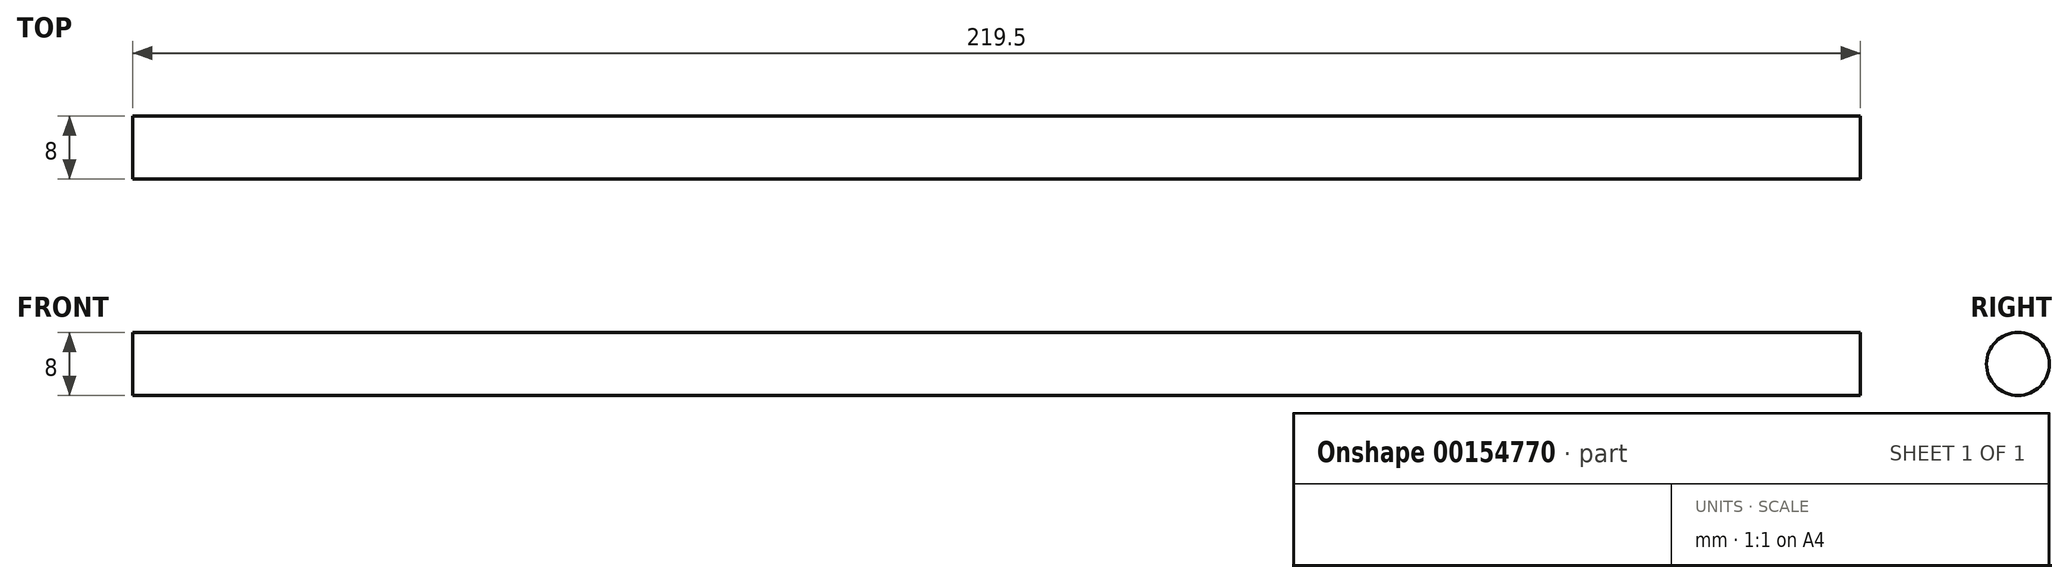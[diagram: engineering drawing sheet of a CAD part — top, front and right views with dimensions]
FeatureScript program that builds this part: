
annotation { "Feature Type Name" : "Feature", "Feature Type Description" : "" }
export const myFeature = defineFeature(function(context is Context, id is Id, definition is map)
    precondition{}
    {
        {
            var Q0;
            Q0=qCreatedBy(makeId("Right.planeOp"),FACE);
            var sketch = newSketch(context, id + "F0", { "sketchPlane" : qUnion([Q0])});
            skCircle(sketch, "E0", {"center": v(0, 0) * mm, "radius": 4 * mm});
            skSolve(sketch);
        }
        {
            var Q0;
            Q0=makeQuery(id+"F0.imprint","IMPRINT",FACE,{"disambiguationData":[TD([[makeQuery(id+"F0.imprint","IMPRINT",EDGE,{"derivedFrom":sQuery(id+"F0.wireOp",EDGE,"E0")}),1.0]])]});
            extrude(context, id + "F1", {"entities" : qUnion([Q0]), "depth" : 219.5 * mm, "symmetric" : true});
        }
    });
